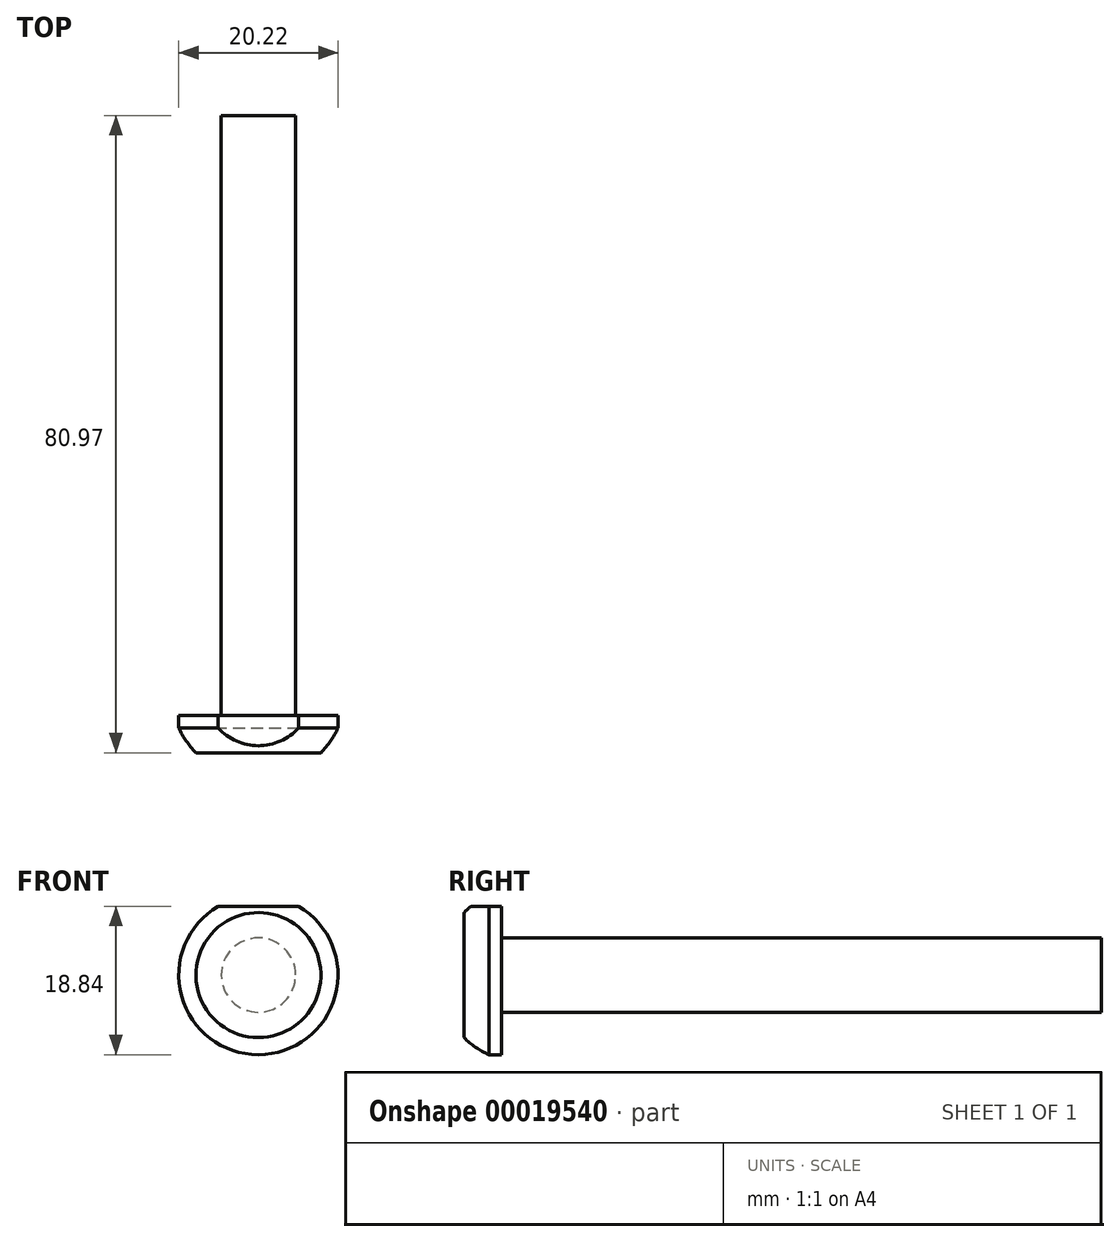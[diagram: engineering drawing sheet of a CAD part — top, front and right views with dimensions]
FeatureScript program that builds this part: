
annotation { "Feature Type Name" : "Feature", "Feature Type Description" : "" }
export const myFeature = defineFeature(function(context is Context, id is Id, definition is map)
    precondition{}
    {
        {
            var Q0;
            Q0=qCreatedBy(makeId("Right.planeOp"),FACE);
            var sketch = newSketch(context, id + "F0", { "sketchPlane" : qUnion([Q0])});
            skLineSegment(sketch, "E0", {"start": v(0, 0) * mm, "end": v(73.19, 0) * mm});
            skLineSegment(sketch, "E1", {"start": v(0, 0) * mm, "end": v(-7.78, 0) * mm});
            skLineSegment(sketch, "E2", {"start": v(-7.78, 7.94) * mm, "end": v(-7.78, 0) * mm});
            skLineSegment(sketch, "E3", {"start": v(-3.01, 10.11) * mm, "end": v(-3.01, 4.72) * mm});
            skLineSegment(sketch, "E4", {"start": v(-4.6, 10.11) * mm, "end": v(-3.01, 10.11) * mm});
            skArc(sketch, "E5.trimOffspring", {"start": v(-4.6, 10.11) * mm, "mid": v(-6.28, 9.16) * mm, "end": v(-7.78, 7.94) * mm});
            skPoint(sketch, "E6.end.orphan", {"position": v(-4.6, 0) * mm});
            skLineSegment(sketch, "E7", {"start": v(-3.01, 4.72) * mm, "end": v(73.19, 4.72) * mm});
            skLineSegment(sketch, "E8", {"start": v(73.19, 4.72) * mm, "end": v(73.19, 0) * mm});
            skPoint(sketch, "E9.orphan", {"position": v(-3.01, 0) * mm});
            skSolve(sketch);
        }
        {
            var Q0;
            Q0 = qSketchRegion(id + "F0", true);
            var Q1;
            Q1=sQuery(id+"F0.wireOp",EDGE,"E0");
            revolve(context, id + "F1", {"entities" : qUnion([Q0]), "axis" : qUnion([Q1]), "revolveType" : RevolveType.FULL});
        }
        {
            var Q0;
            Q0=qCreatedBy(makeId("Right.planeOp"),FACE);
            var sketch = newSketch(context, id + "F2", { "sketchPlane" : qUnion([Q0])});
            skLineSegment(sketch, "E10", {"start": v(0, 8.73) * mm, "end": v(-14.16, 8.73) * mm});
            skLineSegment(sketch, "E11", {"start": v(-14.16, 8.73) * mm, "end": v(-14.16, 18.77) * mm});
            skLineSegment(sketch, "E12", {"start": v(-14.16, 18.77) * mm, "end": v(0, 18.77) * mm});
            skLineSegment(sketch, "E13", {"start": v(0, 18.77) * mm, "end": v(0, 8.73) * mm});
            skSolve(sketch);
        }
        {
            var Q0;
            Q0=makeQuery(id+"F2.imprint","IMPRINT",FACE,{"disambiguationData":[TD([[makeQuery(id+"F2.imprint","IMPRINT",EDGE,{"derivedFrom":sQuery(id+"F2.wireOp",EDGE,"E10")}),-1.0]])]});
            extrude(context, id + "F3", {"entities" : qUnion([Q0]), "operationType" : NewBodyOperationType.REMOVE, "endBound" : BoundingType.THROUGH_ALL, "oppositeDirection" : true, "depth" : 25.4 * mm, "hasSecondDirection" : true, "secondDirectionBound" : SecondDirectionBoundingType.THROUGH_ALL, "secondDirectionOppositeDirection" : false, "secondDirectionDepth" : 25.4 * mm});
        }
    });
